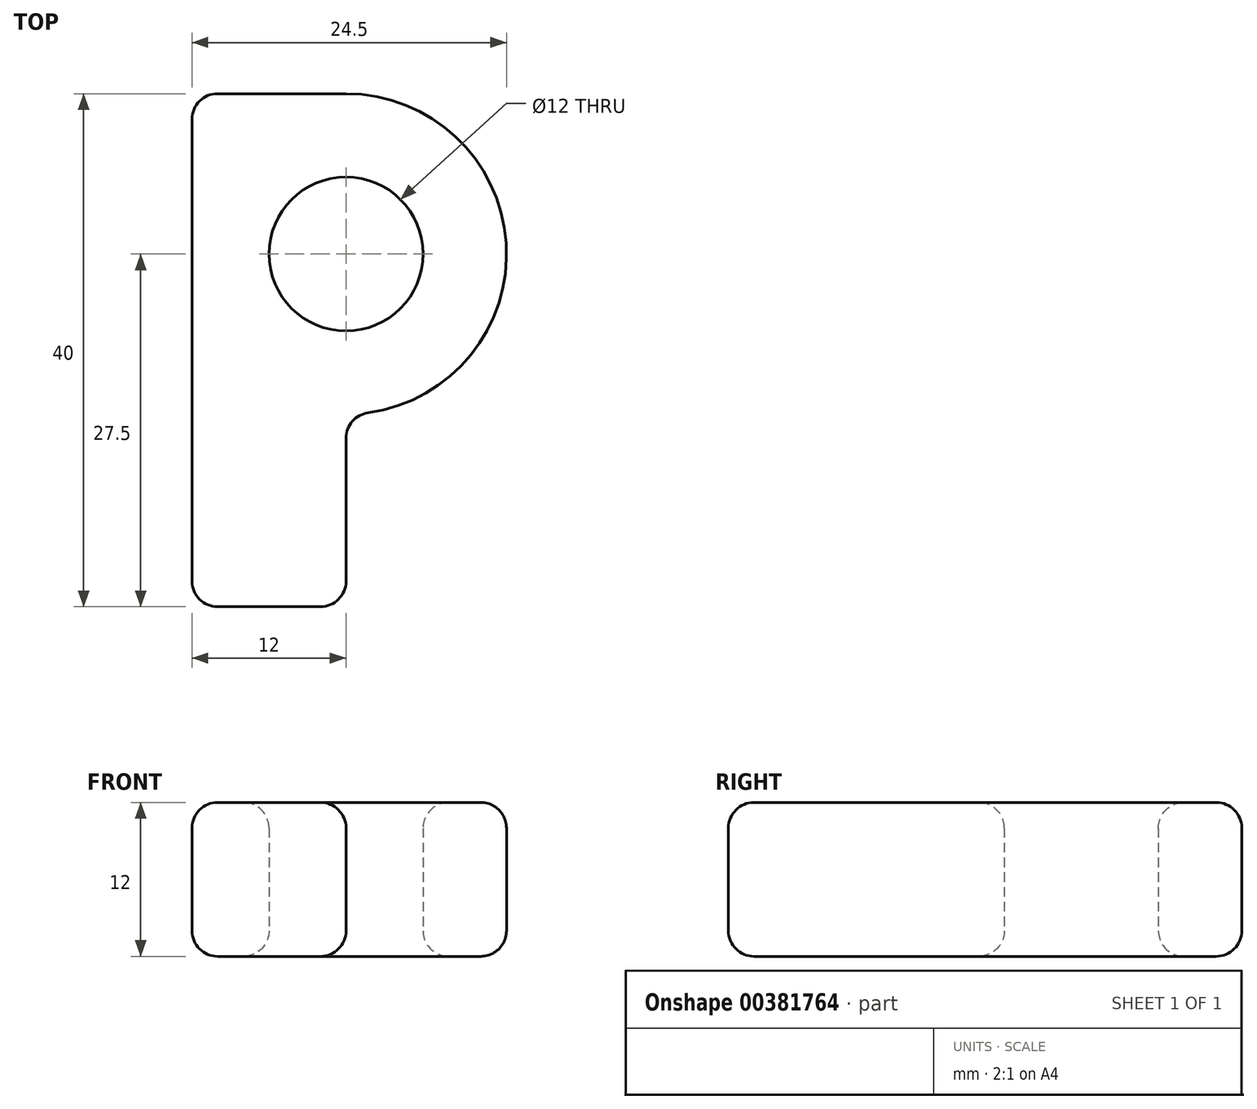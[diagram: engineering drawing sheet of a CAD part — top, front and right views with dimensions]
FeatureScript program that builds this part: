
annotation { "Feature Type Name" : "Feature", "Feature Type Description" : "" }
export const myFeature = defineFeature(function(context is Context, id is Id, definition is map)
    precondition{}
    {
        {
            var Q0;
            Q0=qCreatedBy(makeId("Top.planeOp"),FACE);
            var sketch = newSketch(context, id + "F0", { "sketchPlane" : qUnion([Q0])});
            skLineSegment(sketch, "E0", {"start": v(0, 0) * mm, "end": v(0, 40) * mm});
            skLineSegment(sketch, "E1", {"start": v(0, 40) * mm, "end": v(12, 40) * mm});
            skLineSegment(sketch, "E2", {"start": v(12, 0) * mm, "end": v(0, 0) * mm});
            skArc(sketch, "E3", {"start": v(12, 15) * mm, "mid": v(24.5, 27.5) * mm, "end": v(12, 40) * mm});
            skCircle(sketch, "E4", {"center": v(12, 27.5) * mm, "radius": 6 * mm});
            skLineSegment(sketch, "E5.trimOffspring", {"start": v(12, 15) * mm, "end": v(12, 0) * mm});
            skSolve(sketch);
        }
        {
            var Q0;
            Q0 = qSketchRegion(id + "F0", true);
            extrude(context, id + "F1", {"entities" : qUnion([Q0]), "depth" : 12 * mm});
        }
        {
            var Q0;
            Q0=makeQuery(id+"F1.opExtrude","CAP_FACE",FACE,{"disambiguationData":[OSD([sQuery(id+"F0.wireOp",EDGE,"E0"),sQuery(id+"F0.wireOp",EDGE,"E1"),sQuery(id+"F0.wireOp",EDGE,"E2"),sQuery(id+"F0.wireOp",EDGE,"E3"),sQuery(id+"F0.wireOp",EDGE,"E4"),sQuery(id+"F0.wireOp",EDGE,"E5.trimOffspring")])],"isStart":false});
            var Q1;
            Q1=makeQuery(id+"F1.opExtrude","CAP_FACE",FACE,{"disambiguationData":[OSD([sQuery(id+"F0.wireOp",EDGE,"E0"),sQuery(id+"F0.wireOp",EDGE,"E1"),sQuery(id+"F0.wireOp",EDGE,"E2"),sQuery(id+"F0.wireOp",EDGE,"E3"),sQuery(id+"F0.wireOp",EDGE,"E4"),sQuery(id+"F0.wireOp",EDGE,"E5.trimOffspring")])],"isStart":true});
            var Q2;
            Q2=makeQuery(id+"F1.opExtrude","SWEPT_EDGE",EDGE,{"disambiguationData":[OSD([sQuery(id+"F0.wireOp",EDGE,"E0"),sQuery(id+"F0.wireOp",EDGE,"E1")])]});
            var Q3;
            Q3=makeQuery(id+"F1.opExtrude","SWEPT_EDGE",EDGE,{"disambiguationData":[OSD([sQuery(id+"F0.wireOp",EDGE,"E0"),sQuery(id+"F0.wireOp",EDGE,"E2")])]});
            var Q4;
            Q4=makeQuery(id+"F1.opExtrude","SWEPT_FACE",FACE,{"disambiguationData":[OSD([sQuery(id+"F0.wireOp",EDGE,"E5.trimOffspring")])]});
            fillet(context, id + "F2", {"entities" : qUnion([Q0, Q1, Q2, Q3, Q4]), "radius" : 2 * mm, "tangentPropagation" : true, "allowEdgeOverflow" : false});
        }
    });
